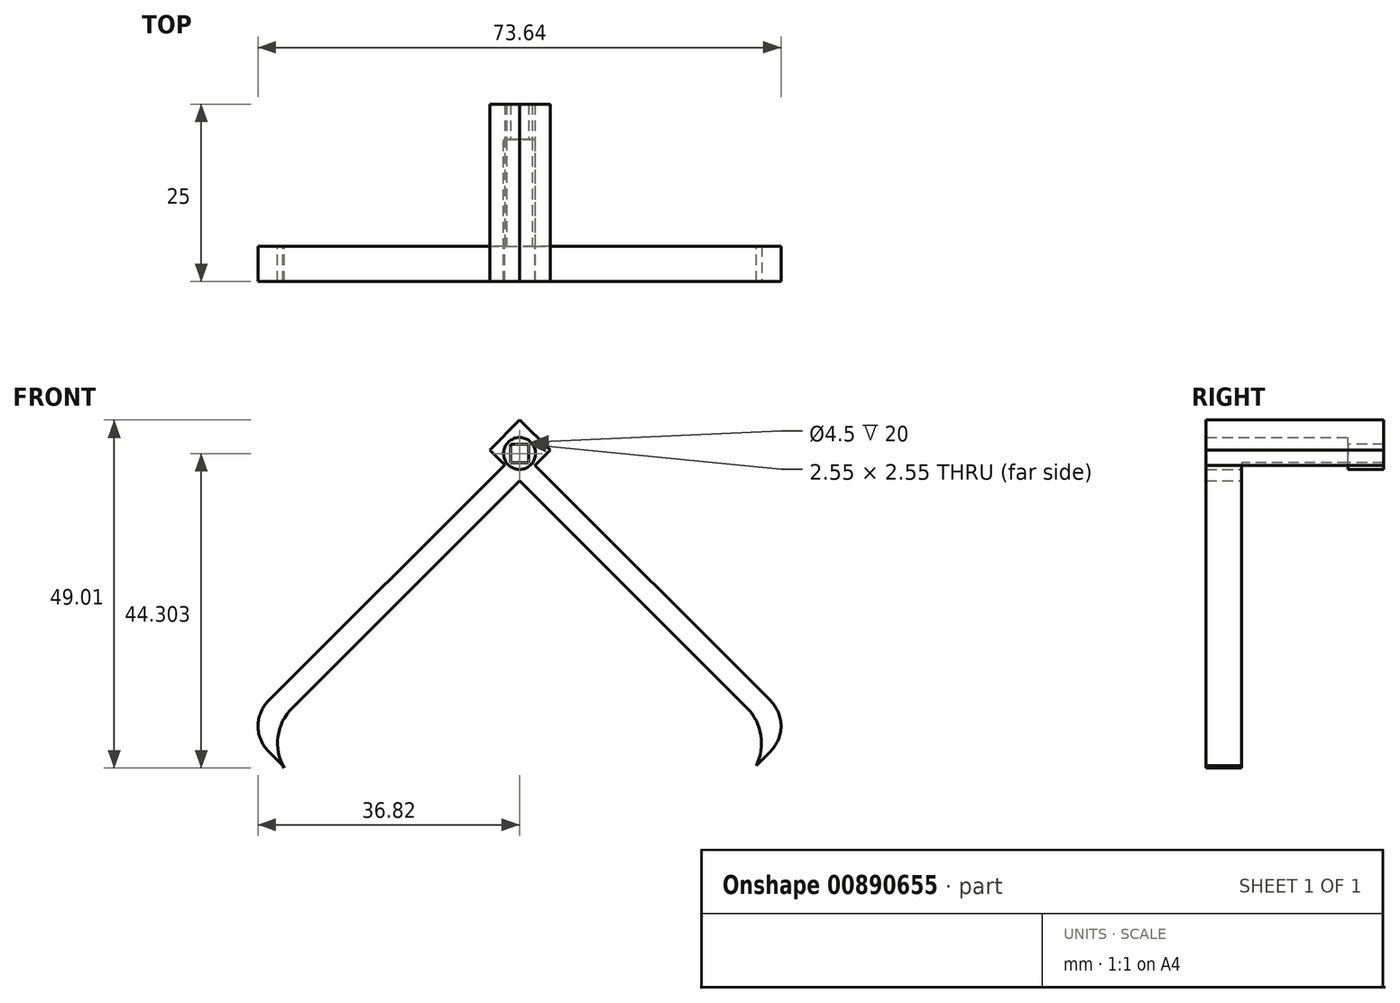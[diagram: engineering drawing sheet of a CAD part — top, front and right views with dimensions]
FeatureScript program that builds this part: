
annotation { "Feature Type Name" : "Feature", "Feature Type Description" : "" }
export const myFeature = defineFeature(function(context is Context, id is Id, definition is map)
    precondition{}
    {
        {
            var Q0;
            Q0=qCreatedBy(makeId("Front.planeOp"),FACE);
            var sketch = newSketch(context, id + "F0", { "sketchPlane" : qUnion([Q0])});
            skLineSegment(sketch, "E0", {"start": v(0, 0) * mm, "end": v(-38.9, -38.9) * mm});
            skLineSegment(sketch, "E1", {"start": v(-38.9, -38.9) * mm, "end": v(-33.32, -44.46) * mm});
            skLineSegment(sketch, "E2", {"start": v(-33.12, -44.8) * mm, "end": v(-33.32, -44.46) * mm});
            skLineSegment(sketch, "E3", {"start": v(-32.02, -36.33) * mm, "end": v(0.07, -4.24) * mm});
            skLineSegment(sketch, "E4", {"start": v(0.07, -4.24) * mm, "end": v(-2.09, -2.09) * mm});
            skLineSegment(sketch, "E5", {"start": v(-2.09, -2.09) * mm, "end": v(0.03, -4.2) * mm});
            skLineSegment(sketch, "E6", {"start": v(0.07, -4.24) * mm, "end": v(2.22, -2.09) * mm});
            skLineSegment(sketch, "E7", {"start": v(0.07, -4.24) * mm, "end": v(-4.18, 0) * mm});
            skLineSegment(sketch, "E8", {"start": v(0.07, -4.24) * mm, "end": v(4.3, 0) * mm});
            skLineSegment(sketch, "E9", {"start": v(-4.18, 0) * mm, "end": v(0.07, 4.24) * mm});
            skLineSegment(sketch, "E10", {"start": v(0.03, 4.2) * mm, "end": v(4.3, 0) * mm});
            skLineSegment(sketch, "E11.MirrorCS", {"start": v(38.9, -38.9) * mm, "end": v(33.32, -44.46) * mm});
            skLineSegment(sketch, "E12.MirrorCS", {"start": v(0, 0) * mm, "end": v(38.9, -38.9) * mm});
            skLineSegment(sketch, "E13.MirrorCS", {"start": v(35.83, -40.14) * mm, "end": v(-0.07, -4.24) * mm});
            skLineSegment(sketch, "E14.MirrorCS", {"start": v(33.32, -44.46) * mm, "end": v(35.83, -40.14) * mm});
            skPoint(sketch, "E15.third.point", {"position": v(0, 2.17) * mm});
            skCircle(sketch, "E16", {"center": v(0, -0.5) * mm, "radius": 1.8 * mm});
            skLineSegment(sketch, "E17.bottom", {"start": v(1.27, 0.78) * mm, "end": v(-1.27, 0.78) * mm});
            skLineSegment(sketch, "E17.top", {"start": v(1.27, -1.77) * mm, "end": v(-1.27, -1.77) * mm});
            skLineSegment(sketch, "E17.left", {"start": v(1.27, 0.78) * mm, "end": v(1.27, -1.77) * mm});
            skLineSegment(sketch, "E17.right", {"start": v(-1.27, 0.78) * mm, "end": v(-1.27, -1.77) * mm});
            skCircle(sketch, "E18", {"center": v(0, -0.5) * mm, "radius": 2.25 * mm});
            skPoint(sketch, "E19.visualSharp", {"position": v(-35.83, -40.14) * mm});
            skArc(sketch, "E19.filletArc", {"start": v(-32.02, -36.33) * mm, "mid": v(-34.01, -40.38) * mm, "end": v(-33.12, -44.8) * mm});
            skSolve(sketch);
        }
        {
            var Q0;
            Q0=qSketchRegion(id+"F0",true);
            var Q1;
            {var subQ0=sQuery(id+"F0.wireOp",EDGE,"0f1ebc3f-252f-488c-8a79-436134c23e0f.1");Q1=makeQuery(id+"F0.imprint","IMPRINT",FACE,{"disambiguationData":[TD([[makeQuery(id+"F0.imprint","IMPRINT",EDGE,{"derivedFrom":subQ0}),-1.0]])]});}
            extrude(context, id + "F1", {"entities" : qUnion([Q0, Q1]), "depth" : 5 * mm, "offsetDistance" : 25 * mm});
        }
        {
            var Q0;
            {var subQ12=sQuery(id+"F0.wireOp",EDGE,"E9");Q0=makeQuery(id+"F0.imprint","IMPRINT",FACE,{"disambiguationData":[TD([[makeQuery(id+"F0.imprint","IMPRINT",EDGE,{"derivedFrom":subQ12}),-1.0]])]});}
            var Q1;
            {var subQ1=sQuery(id+"F0.wireOp",EDGE,"E7");var subQ10=makeQuery(id+"F0.imprint","IMPRINT",VERTEX,{"derivedFrom":subQ1});Q1=makeQuery(id+"F0.imprint","IMPRINT",FACE,{"disambiguationData":[TD([[makeQuery(id+"F0.imprint","IMPRINT",EDGE,{"disambiguationData":[TD([[subQ10,-1.0]])],"derivedFrom":subQ1}),-1.0]])]});}
            extrude(context, id + "F2", {"entities" : qUnion([Q0, Q1]), "operationType" : NewBodyOperationType.ADD, "oppositeDirection" : true, "depth" : 20 * mm, "offsetDistance" : 25 * mm});
        }
        {
            var Q0;
            Q0=makeQuery(id+"F1.opExtrude","SWEPT_EDGE",EDGE,{"disambiguationData":[OSD([sQuery(id+"F0.wireOp",EDGE,"E11.MirrorCS"),sQuery(id+"F0.wireOp",EDGE,"E12.MirrorCS")])]});
            var Q1;
            Q1=makeQuery(id+"F1.opExtrude","SWEPT_EDGE",EDGE,{"disambiguationData":[OSD([sQuery(id+"F0.wireOp",EDGE,"E0"),sQuery(id+"F0.wireOp",EDGE,"E1")])]});
            fillet(context, id + "F3", {"entities" : qUnion([Q0, Q1]), "radius" : 5 * mm, "tangentPropagation" : true, "allowEdgeOverflow" : false});
        }
        {
            var Q0;
            {var subQ0=sQuery(id+"F0.wireOp",EDGE,"f05015f5-0773-4215-b776-3aad7731f361.0");Q0=makeQuery(id+"F0.imprint","IMPRINT",FACE,{"disambiguationData":[TD([[makeQuery(id+"F0.imprint","IMPRINT",EDGE,{"derivedFrom":subQ0}),1.0]])]});}
            var Q1;
            {var subQ0=sQuery(id+"F0.wireOp",EDGE,"f05015f5-0773-4215-b776-3aad7731f361.1");Q1=makeQuery(id+"F0.imprint","IMPRINT",FACE,{"disambiguationData":[TD([[makeQuery(id+"F0.imprint","IMPRINT",EDGE,{"derivedFrom":subQ0}),1.0]])]});}
            var Q2;
            {var subQ0=sQuery(id+"F0.wireOp",EDGE,"f05015f5-0773-4215-b776-3aad7731f361.5");Q2=makeQuery(id+"F0.imprint","IMPRINT",FACE,{"disambiguationData":[TD([[makeQuery(id+"F0.imprint","IMPRINT",EDGE,{"derivedFrom":subQ0}),1.0]])]});}
            var Q3;
            {var subQ0=sQuery(id+"F0.wireOp",EDGE,"f05015f5-0773-4215-b776-3aad7731f361.4");Q3=makeQuery(id+"F0.imprint","IMPRINT",FACE,{"disambiguationData":[TD([[makeQuery(id+"F0.imprint","IMPRINT",EDGE,{"derivedFrom":subQ0}),1.0]])]});}
            var Q4;
            {var subQ0=sQuery(id+"F0.wireOp",EDGE,"E17.left");var subQ1=sQuery(id+"F0.wireOp",EDGE,"E12.MirrorCS");var subQ2=makeQuery(id+"F0.imprint","INTERSECT",VERTEX,{"derivedFrom":[subQ1,subQ0]});Q4=makeQuery(id+"F0.imprint","IMPRINT",FACE,{"disambiguationData":[TD([[makeQuery(id+"F0.imprint","IMPRINT",EDGE,{"disambiguationData":[TD([[subQ2,-1.0]])],"derivedFrom":subQ1}),1.0]])]});}
            var Q5;
            {var subQ0=sQuery(id+"F0.wireOp",EDGE,"E17.left");var subQ1=sQuery(id+"F0.wireOp",EDGE,"E12.MirrorCS");var subQ2=makeQuery(id+"F0.imprint","INTERSECT",VERTEX,{"derivedFrom":[subQ1,subQ0]});Q5=makeQuery(id+"F0.imprint","IMPRINT",FACE,{"disambiguationData":[TD([[makeQuery(id+"F0.imprint","IMPRINT",EDGE,{"disambiguationData":[TD([[subQ2,-1.0]])],"derivedFrom":subQ1}),-1.0]])]});}
            var Q6;
            {var subQ0=sQuery(id+"F0.wireOp",EDGE,"E17.right");var subQ1=sQuery(id+"F0.wireOp",EDGE,"E0");var subQ2=makeQuery(id+"F0.imprint","INTERSECT",VERTEX,{"derivedFrom":[subQ1,subQ0]});Q6=makeQuery(id+"F0.imprint","IMPRINT",FACE,{"disambiguationData":[TD([[makeQuery(id+"F0.imprint","IMPRINT",EDGE,{"disambiguationData":[TD([[subQ2,-1.0]])],"derivedFrom":subQ1}),1.0]])]});}
            var Q7;
            {var subQ0=sQuery(id+"F0.wireOp",EDGE,"E17.top");Q7=makeQuery(id+"F0.imprint","IMPRINT",FACE,{"disambiguationData":[TD([[makeQuery(id+"F0.imprint","IMPRINT",EDGE,{"derivedFrom":subQ0}),1.0]])]});}
            var Q8;
            {var subQ0=sQuery(id+"F0.wireOp",EDGE,"E17.right");var subQ1=sQuery(id+"F0.wireOp",EDGE,"E0");var subQ2=makeQuery(id+"F0.imprint","INTERSECT",VERTEX,{"derivedFrom":[subQ1,subQ0]});Q8=makeQuery(id+"F0.imprint","IMPRINT",FACE,{"disambiguationData":[TD([[makeQuery(id+"F0.imprint","IMPRINT",EDGE,{"disambiguationData":[TD([[subQ2,-1.0]])],"derivedFrom":subQ1}),-1.0]])]});}
            var Q9;
            {var subQ0=sQuery(id+"F0.wireOp",EDGE,"E17.bottom");Q9=makeQuery(id+"F0.imprint","IMPRINT",FACE,{"disambiguationData":[TD([[makeQuery(id+"F0.imprint","IMPRINT",EDGE,{"derivedFrom":subQ0}),-1.0]])]});}
            var Q10;
            {var subQ1=sQuery(id+"F0.wireOp",EDGE,"E16");var subQ3=sQuery(id+"F0.wireOp",EDGE,"E0");var subQ4=makeQuery(id+"F0.imprint","INTERSECT",VERTEX,{"derivedFrom":[subQ3,subQ1]});Q10=makeQuery(id+"F0.imprint","IMPRINT",FACE,{"disambiguationData":[TD([[makeQuery(id+"F0.imprint","IMPRINT",EDGE,{"disambiguationData":[TD([[subQ4,-1.0]])],"derivedFrom":subQ3}),-1.0]])]});}
            var Q11;
            {var subQ1=sQuery(id+"F0.wireOp",EDGE,"E16");var subQ4=sQuery(id+"F0.wireOp",EDGE,"E0");var subQ5=makeQuery(id+"F0.imprint","INTERSECT",VERTEX,{"derivedFrom":[subQ4,subQ1]});Q11=makeQuery(id+"F0.imprint","IMPRINT",FACE,{"disambiguationData":[TD([[makeQuery(id+"F0.imprint","IMPRINT",EDGE,{"disambiguationData":[TD([[subQ5,-1.0]])],"derivedFrom":subQ4}),1.0]])]});}
            var Q12;
            Q12=makeQuery(id+"F2.opExtrude","CAP_FACE",FACE,{"disambiguationData":[OSD([sQuery(id+"F0.wireOp",EDGE,"E7"),sQuery(id+"F0.wireOp",EDGE,"E8"),sQuery(id+"F0.wireOp",EDGE,"E9"),sQuery(id+"F0.wireOp",EDGE,"E10"),sQuery(id+"F0.wireOp",EDGE,"b2553523-69ed-4fd1-b225-77e335340f50.filletArc"),sQuery(id+"F0.wireOp",EDGE,"E16")])],"isStart":false});
            extrude(context, id + "F4", {"entities" : qUnion([Q0, Q1, Q2, Q3, Q4, Q5, Q6, Q7, Q8, Q9, Q10, Q11]), "operationType" : NewBodyOperationType.ADD, "endBound" : BoundingType.UP_TO_SURFACE, "oppositeDirection" : true, "depth" : 25 * mm, "endBoundEntityFace" : qUnion([Q12]), "offsetDistance" : 10 * mm, "hasSecondDirection" : true, "secondDirectionOppositeDirection" : true, "secondDirectionDepth" : 15 * mm});
        }
        {
            var Q0;
            Q0=makeQuery(id+"F1.opExtrude","SWEPT_EDGE",EDGE,{"disambiguationData":[OSD([sQuery(id+"F0.wireOp",EDGE,"E13.MirrorCS"),sQuery(id+"F0.wireOp",EDGE,"E14.MirrorCS")])]});
            fillet(context, id + "F5", {"entities" : qUnion([Q0]), "radius" : 7 * mm, "tangentPropagation" : true, "allowEdgeOverflow" : false});
        }
    });
